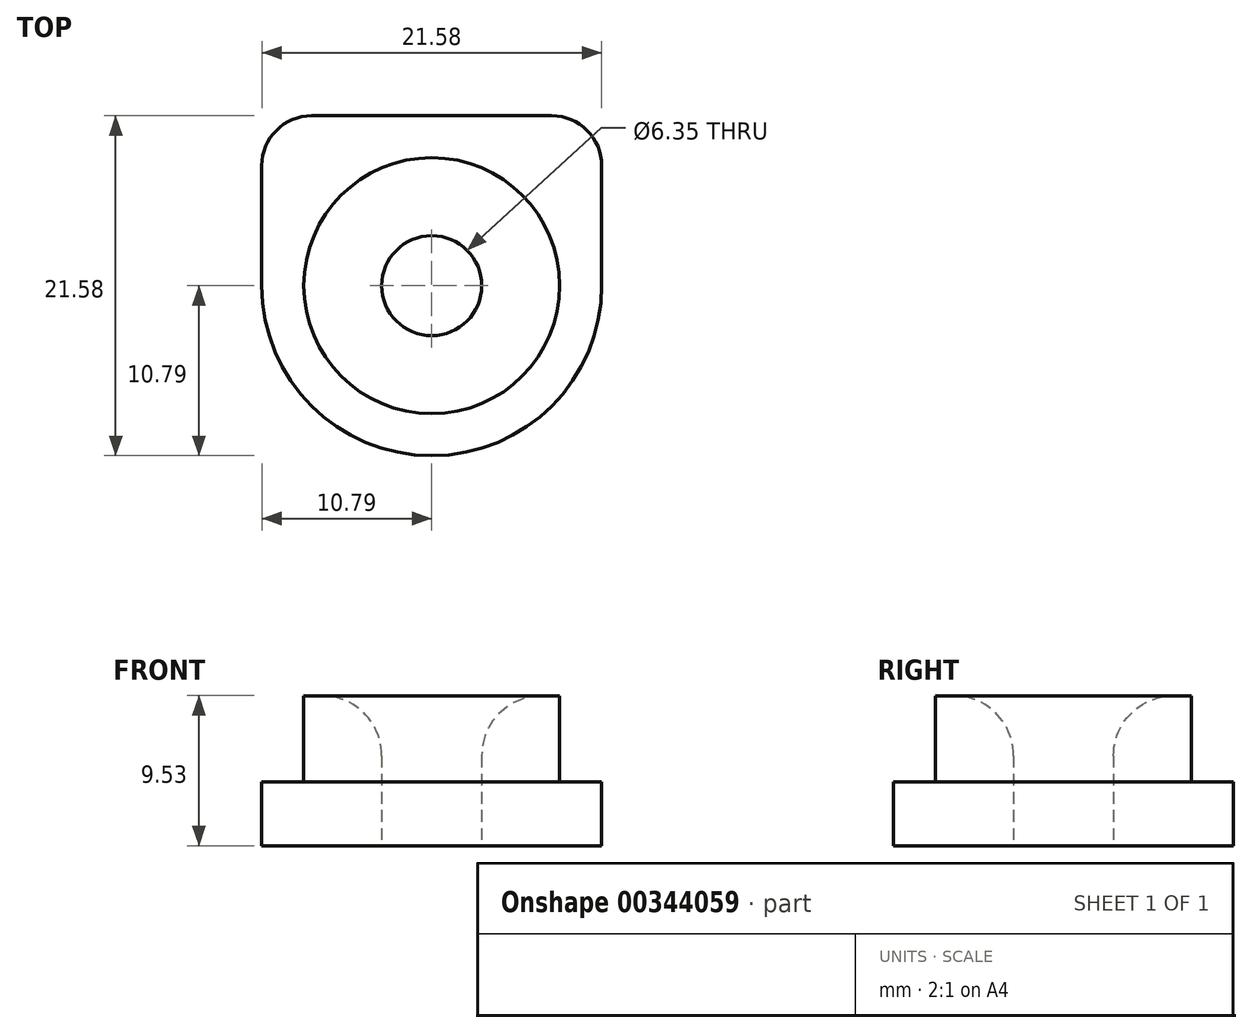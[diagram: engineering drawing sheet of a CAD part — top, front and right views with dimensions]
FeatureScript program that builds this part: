
annotation { "Feature Type Name" : "Feature", "Feature Type Description" : "" }
export const myFeature = defineFeature(function(context is Context, id is Id, definition is map)
    precondition{}
    {
        {
            var Q0;
            Q0=qCreatedBy(makeId("Top.planeOp"),FACE);
            var sketch = newSketch(context, id + "F0", { "sketchPlane" : qUnion([Q0])});
            skCircle(sketch, "E0", {"center": v(0, 0) * mm, "radius": 10.8 * mm});
            skCircle(sketch, "E1", {"center": v(0, 0) * mm, "radius": 8.13 * mm});
            skCircle(sketch, "E2", {"center": v(0, 0) * mm, "radius": 3.18 * mm});
            skLineSegment(sketch, "E3.bottom", {"start": v(-10.8, 0) * mm, "end": v(10.8, 0) * mm});
            skLineSegment(sketch, "E3.top", {"start": v(-7.62, 10.8) * mm, "end": v(7.62, 10.8) * mm});
            skLineSegment(sketch, "E3.left", {"start": v(-10.8, 0) * mm, "end": v(-10.8, 7.62) * mm});
            skLineSegment(sketch, "E3.right", {"start": v(10.8, 0) * mm, "end": v(10.8, 7.62) * mm});
            skPoint(sketch, "E4.visualSharp", {"position": v(-10.8, 10.8) * mm});
            skArc(sketch, "E4.filletArc", {"start": v(-7.62, 10.8) * mm, "mid": v(-9.87, 9.87) * mm, "end": v(-10.8, 7.62) * mm});
            skPoint(sketch, "E5.visualSharp", {"position": v(10.8, 10.8) * mm});
            skArc(sketch, "E5.filletArc", {"start": v(10.8, 7.62) * mm, "mid": v(9.87, 9.87) * mm, "end": v(7.62, 10.8) * mm});
            skSolve(sketch);
        }
        {
            var Q0;
            {var subQ0=sQuery(id+"F0.wireOp",EDGE,"E3.bottom");var subQ3=sQuery(id+"F0.wireOp",EDGE,"E1");var subQ4=makeQuery(id+"F0.imprint","INTERSECT",VERTEX,{"disambiguationData":[OD(0.0)],"derivedFrom":[subQ3,subQ0]});Q0=makeQuery(id+"F0.imprint","IMPRINT",FACE,{"disambiguationData":[TD([[makeQuery(id+"F0.imprint","IMPRINT",EDGE,{"disambiguationData":[TD([[subQ4,1.0]])],"derivedFrom":subQ3}),-1.0]])]});}
            var Q1;
            {var subQ0=sQuery(id+"F0.wireOp",EDGE,"E3.bottom");var subQ4=sQuery(id+"F0.wireOp",EDGE,"E1");var subQ5=makeQuery(id+"F0.imprint","INTERSECT",VERTEX,{"disambiguationData":[OD(0.0)],"derivedFrom":[subQ4,subQ0]});Q1=makeQuery(id+"F0.imprint","IMPRINT",FACE,{"disambiguationData":[TD([[makeQuery(id+"F0.imprint","IMPRINT",EDGE,{"disambiguationData":[TD([[subQ5,-1.0]])],"derivedFrom":subQ4}),-1.0]])]});}
            var Q2;
            {var subQ0=sQuery(id+"F0.wireOp",EDGE,"E3.left");Q2=makeQuery(id+"F0.imprint","IMPRINT",FACE,{"disambiguationData":[TD([[makeQuery(id+"F0.imprint","IMPRINT",EDGE,{"derivedFrom":subQ0}),-1.0]])]});}
            var Q3;
            {var subQ0=sQuery(id+"F0.wireOp",EDGE,"E3.right");Q3=makeQuery(id+"F0.imprint","IMPRINT",FACE,{"disambiguationData":[TD([[makeQuery(id+"F0.imprint","IMPRINT",EDGE,{"derivedFrom":subQ0}),1.0]])]});}
            extrude(context, id + "F1", {"entities" : qUnion([Q0, Q1, Q2, Q3]), "depth" : 4.06 * mm});
        }
        {
            var Q0;
            {var subQ0=sQuery(id+"F0.wireOp",EDGE,"E3.bottom");var subQ1=sQuery(id+"F0.wireOp",EDGE,"E1");var subQ2=makeQuery(id+"F0.imprint","INTERSECT",VERTEX,{"disambiguationData":[OD(0.0)],"derivedFrom":[subQ1,subQ0]});Q0=makeQuery(id+"F0.imprint","IMPRINT",FACE,{"disambiguationData":[TD([[makeQuery(id+"F0.imprint","IMPRINT",EDGE,{"disambiguationData":[TD([[subQ2,-1.0]])],"derivedFrom":subQ1}),1.0]])]});}
            var Q1;
            {var subQ0=sQuery(id+"F0.wireOp",EDGE,"E3.bottom");var subQ1=sQuery(id+"F0.wireOp",EDGE,"E1");var subQ2=makeQuery(id+"F0.imprint","INTERSECT",VERTEX,{"disambiguationData":[OD(0.0)],"derivedFrom":[subQ1,subQ0]});Q1=makeQuery(id+"F0.imprint","IMPRINT",FACE,{"disambiguationData":[TD([[makeQuery(id+"F0.imprint","IMPRINT",EDGE,{"disambiguationData":[TD([[subQ2,1.0]])],"derivedFrom":subQ1}),1.0]])]});}
            extrude(context, id + "F2", {"entities" : qUnion([Q0, Q1]), "operationType" : NewBodyOperationType.ADD, "depth" : 9.52 * mm});
        }
        {
            var Q0;
            Q0=makeQuery(id+"F2.opExtrude","CAP_EDGE",EDGE,{"disambiguationData":[OSD([sQuery(id+"F0.wireOp",EDGE,"E2")])],"isStart":false});
            fillet(context, id + "F3", {"entities" : qUnion([Q0]), "radius" : 3.8 * mm, "tangentPropagation" : true, "allowEdgeOverflow" : false});
        }
    });
